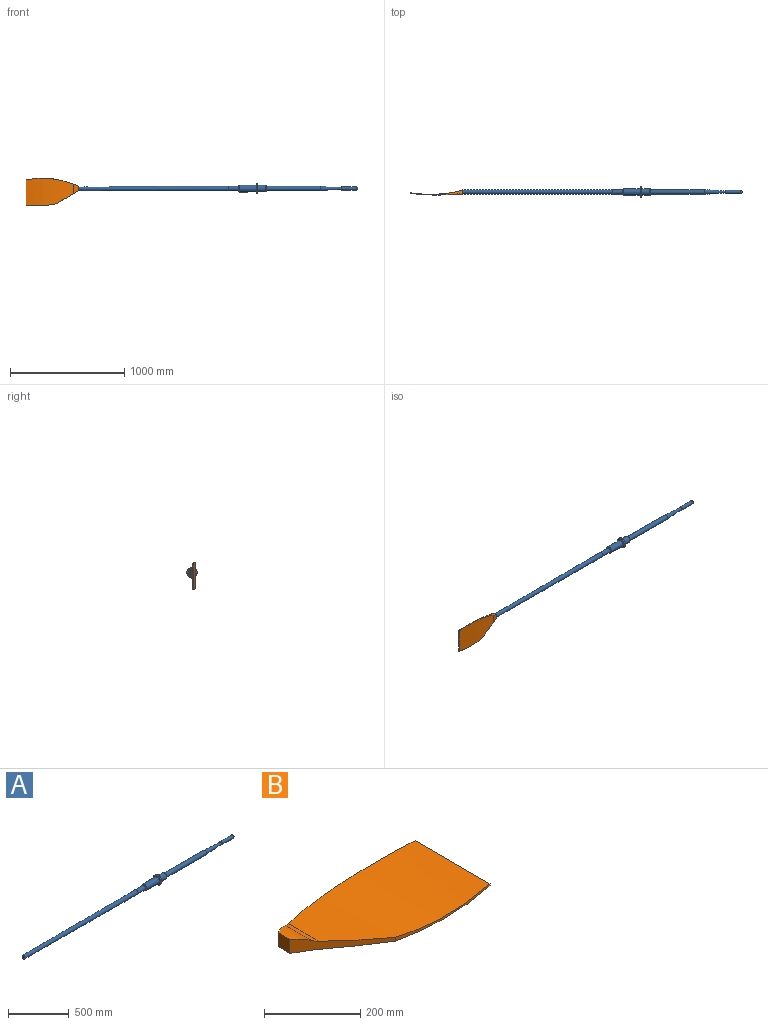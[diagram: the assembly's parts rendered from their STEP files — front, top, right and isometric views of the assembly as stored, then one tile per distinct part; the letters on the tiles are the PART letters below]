
ASSEMBLY  parts=2 mates=1
PART A: 17 faces, bbox 2440x90x90 mm
  f0: cone r=30mm half-angle=45deg, axis (-1,0,0), area 1439.5mm2, adj f6,f12
  f1: cone r=24mm half-angle=45deg, axis (1,0,0), area 1439.5mm2, adj f8,f11
  f2: cylinder r=21mm len=470mm, axis (-1,0,0), area 62015mm2, adj f3,f12
  f3: cone r=10mm half-angle=3.4deg, axis (-1,0,0), area 18048.9mm2, adj f2,f15
  f4: cylinder r=15mm len=130mm, axis (-1,0,0), area 12252.2mm2, adj f5,f15
  f5: sphere r=15mm, area 1413.7mm2, adj f4
  f6: cylinder r=30mm len=69mm, axis (-1,0,0), area 13006.2mm2, adj f0,f14
  f7: cylinder r=45mm len=90mm, axis (-1,0,0), area 4241.2mm2, adj f13,f14
  f8: cylinder r=30mm len=144mm, axis (-1,0,0), area 27143.4mm2, adj f1,f13
  f9: cone r=21mm half-angle=0.2deg, axis (1,0,0), area 158446.8mm2, adj f10,f16
  f10: cylinder r=21mm len=90mm, axis (-1,0,0), area 11875.2mm2, adj f9,f11
  f11: plane 48x48mm, normal (-1,0,0), area 424.1mm2, adj f1,f10
  f12: plane 48x48mm, normal (1,0,0), area 424.1mm2, adj f0,f2
  f13: plane 90x90mm, normal (-1,0,0), area 3534.3mm2, adj f7,f8
  f14: plane 90x90mm, normal (1,0,0), area 3534.3mm2, adj f6,f7
  f15: plane 30x30mm, normal (-1,0,0), area 392.7mm2, adj f3,f4
  f16: plane 35x35mm, normal (-1,0,0), area 962.1mm2, adj f9
PART B: 10 faces, bbox 460.7x240.8x44.8 mm
  f0: plane 35x35mm, normal (-1,0,0), area 1225mm2, adj f1,f4,f5,f8
  f1: cylinder r=716.78mm len=460mm, axis (0,0,-1), area 5243.2mm2, adj f0,f2,f5,f6,f7,f8,f9
  f2: plane 220x5.01mm, normal (1,0,0), area 1103.2mm2, adj f1,f3,f6,f7
  f3: cylinder r=850mm len=265mm, axis (0,0,-1), area 1466mm2, adj f2,f4,f6,f7
  f4: plane 195.75x115.75mm, normal (-0.51,-0.86,0), area 4191.4mm2, adj f0,f3,f5,f6,f7,f8,f9
  f5: cylinder r=86.84mm len=75.91mm, axis (0,1,0), area 2273mm2, adj f0,f1,f4,f9
  f6: cylinder r=1196.24mm len=406.81mm, axis (0,1,0), area 73532.5mm2, adj f1,f2,f3,f4,f9
  f7: cylinder r=1858.89mm len=415.04mm, axis (0,1,0), area 73526.4mm2, adj f1,f2,f3,f4,f8
  f8: plane 81.56x44.96mm, normal (0,0,-1), area 2634.4mm2, adj f0,f1,f4,f7
  f9: cylinder r=50mm len=89.69mm, axis (0,1,0), area 1224.4mm2, adj f1,f4,f5,f6
PLACE A at identity fixed
PLACE B rot(axis=(0,-0.71,-0.71),180deg) t=(0,-1000,500)mm
MATE fastened B.f0 <-> A.f3  axis (1,0,0) through (0,0,500)mm
